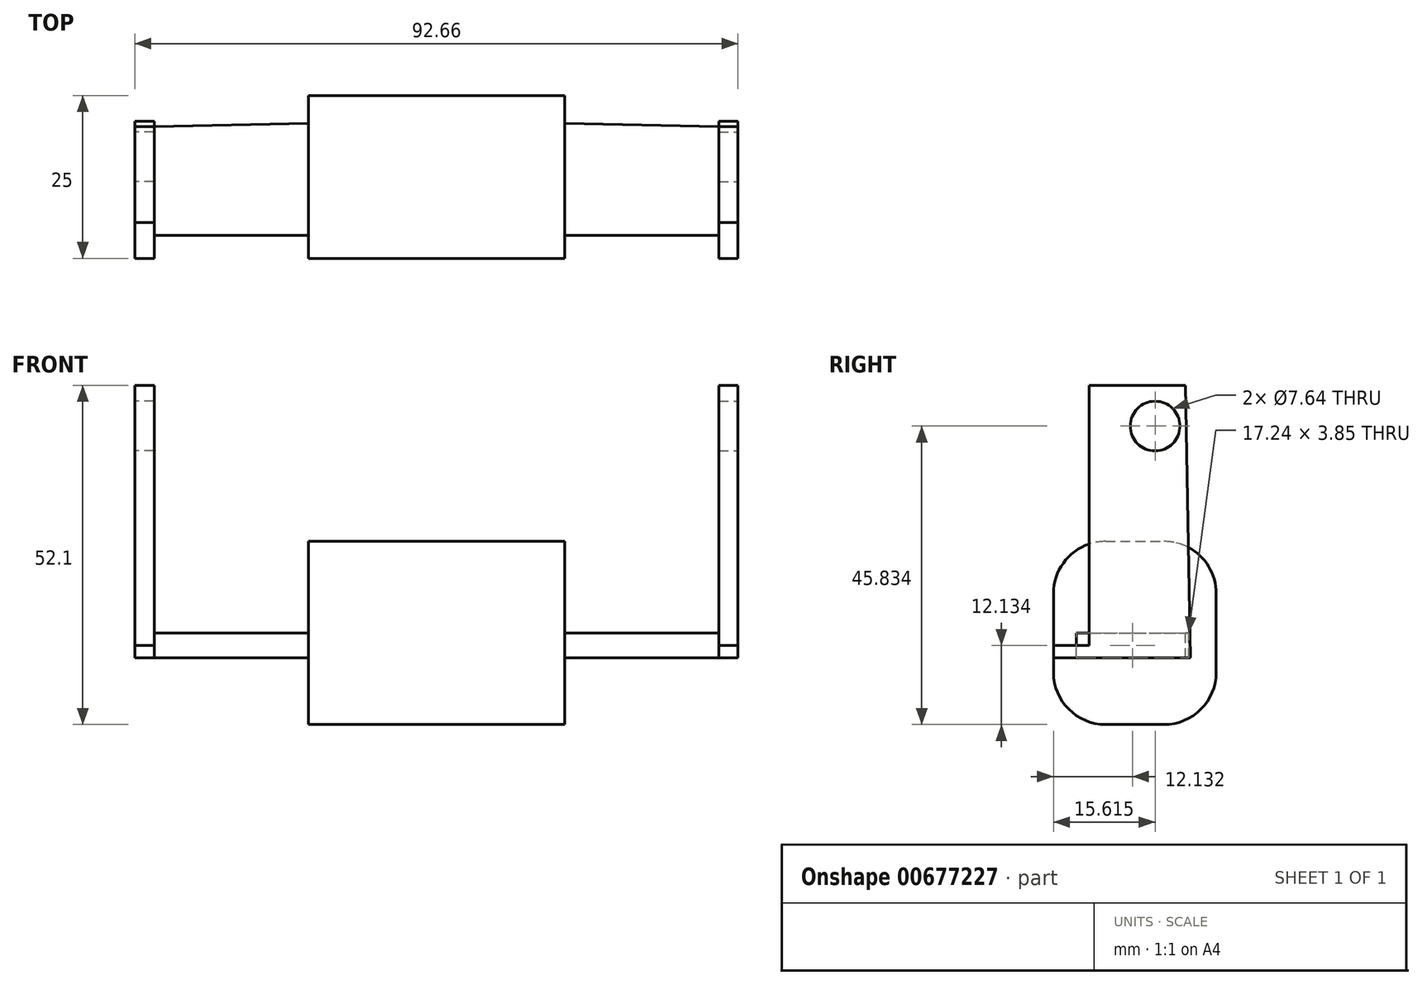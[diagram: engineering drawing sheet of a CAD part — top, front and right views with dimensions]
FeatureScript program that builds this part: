
annotation { "Feature Type Name" : "Feature", "Feature Type Description" : "" }
export const myFeature = defineFeature(function(context is Context, id is Id, definition is map)
    precondition{}
    {
        {
            var Q0;
            Q0=qCreatedBy(makeId("Front.planeOp"),FACE);
            var sketch = newSketch(context, id + "F0", { "sketchPlane" : qUnion([Q0])});
            skLineSegment(sketch, "E0", {"start": v(0, 17.91) * mm, "end": v(-19.69, 17.91) * mm});
            skLineSegment(sketch, "E1", {"start": v(-19.69, 17.91) * mm, "end": v(-19.69, -10.21) * mm});
            skLineSegment(sketch, "E2", {"start": v(-19.69, -10.21) * mm, "end": v(0, -10.21) * mm});
            skLineSegment(sketch, "E3", {"start": v(0, -10.21) * mm, "end": v(0, 17.91) * mm});
            skLineSegment(sketch, "E4", {"start": v(-19.69, 3.85) * mm, "end": v(-43.37, 3.85) * mm});
            skLineSegment(sketch, "E5", {"start": v(-43.37, 3.85) * mm, "end": v(-43.37, 41.9) * mm});
            skLineSegment(sketch, "E6", {"start": v(-43.37, 41.9) * mm, "end": v(-46.33, 41.9) * mm});
            skLineSegment(sketch, "E7", {"start": v(-46.33, 41.9) * mm, "end": v(-46.33, 0) * mm});
            skLineSegment(sketch, "E8", {"start": v(-46.33, 0) * mm, "end": v(-19.69, 0) * mm});
            skSolve(sketch);
        }
        {
            var Q0;
            Q0 = qSketchRegion(id + "F0", true);
            extrude(context, id + "F1", {"entities" : qUnion([Q0]), "depth" : 25 * mm, "offsetDistance" : 25 * mm});
        }
        {
            var Q0;
            Q0=makeQuery(id+"F1.opExtrude","CAP_EDGE",EDGE,{"disambiguationData":[OSD([sQuery(id+"F0.wireOp",EDGE,"E0")])],"isStart":true});
            var Q1;
            Q1=makeQuery(id+"F1.opExtrude","CAP_EDGE",EDGE,{"disambiguationData":[OSD([sQuery(id+"F0.wireOp",EDGE,"E2")])],"isStart":true});
            var Q2;
            Q2=makeQuery(id+"F1.opExtrude","CAP_EDGE",EDGE,{"disambiguationData":[OSD([sQuery(id+"F0.wireOp",EDGE,"E2")])],"isStart":false});
            var Q3;
            Q3=makeQuery(id+"F1.opExtrude","CAP_EDGE",EDGE,{"disambiguationData":[OSD([sQuery(id+"F0.wireOp",EDGE,"E0")])],"isStart":false});
            fillet(context, id + "F2", {"entities" : qUnion([Q0, Q1, Q2, Q3]), "radius" : 8 * mm, "tangentPropagation" : true, "allowEdgeOverflow" : false});
        }
        {
            var Q0;
            Q0=makeQuery(id+"F1.opExtrude","SWEPT_FACE",FACE,{"disambiguationData":[OSD([sQuery(id+"F0.wireOp",EDGE,"E4")])]});
            var sketch = newSketch(context, id + "F3", { "sketchPlane" : qUnion([Q0])});
            skLineSegment(sketch, "E9", {"start": v(-19.69, -21.49) * mm, "end": v(-43.37, -21.49) * mm});
            skLineSegment(sketch, "E10", {"start": v(-43.37, -21.49) * mm, "end": v(-43.37, -25) * mm});
            skLineSegment(sketch, "E11", {"start": v(-43.37, -25) * mm, "end": v(-19.69, -25) * mm});
            skLineSegment(sketch, "E12", {"start": v(-19.69, -25) * mm, "end": v(-19.69, -21.49) * mm});
            skLineSegment(sketch, "E13", {"start": v(-19.69, -4.25) * mm, "end": v(-43.37, -4.75) * mm});
            skLineSegment(sketch, "E14", {"start": v(-43.37, -4.75) * mm, "end": v(-43.37, 0) * mm});
            skLineSegment(sketch, "E15", {"start": v(-43.37, 0) * mm, "end": v(-20.53, 0) * mm});
            skLineSegment(sketch, "E16", {"start": v(-20.53, 0) * mm, "end": v(-19.69, 0) * mm});
            skLineSegment(sketch, "E17", {"start": v(-19.69, 0) * mm, "end": v(-19.69, -4.25) * mm});
            skSolve(sketch);
        }
        {
            var Q0;
            Q0 = qSketchRegion(id + "F3", true);
            extrude(context, id + "F4", {"entities" : qUnion([Q0]), "operationType" : NewBodyOperationType.REMOVE, "oppositeDirection" : true, "depth" : 25 * mm, "offsetDistance" : 25 * mm});
        }
        {
            var Q0;
            Q0=makeQuery(id+"F4.boolean.opBoolean","MERGE",FACE,{"derivedFrom":[makeQuery(id+"F1.opExtrude","SWEPT_FACE",FACE,{"disambiguationData":[OSD([sQuery(id+"F0.wireOp",EDGE,"E5")])]}),makeQuery(id+"F4.opExtrude","SWEPT_FACE",FACE,{"disambiguationData":[OSD([sQuery(id+"F3.wireOp",EDGE,"E10")])]}),makeQuery(id+"F4.opExtrude","SWEPT_FACE",FACE,{"disambiguationData":[OSD([sQuery(id+"F3.wireOp",EDGE,"E14")])]})]});
            var sketch = newSketch(context, id + "F5", { "sketchPlane" : qUnion([Q0])});
            skLineSegment(sketch, "E18", {"start": v(-25, 41.9) * mm, "end": v(-19.53, 41.9) * mm});
            skLineSegment(sketch, "E19", {"start": v(-19.53, 41.9) * mm, "end": v(-19.53, 1.92) * mm});
            skPoint(sketch, "E19.endSnap0", {"position": v(-21.49, 1.92) * mm});
            skLineSegment(sketch, "E20", {"start": v(-19.53, 1.92) * mm, "end": v(-25, 1.92) * mm});
            skLineSegment(sketch, "E21", {"start": v(-25, 1.92) * mm, "end": v(-25, 41.9) * mm});
            skLineSegment(sketch, "E22", {"start": v(-4.75, 41.9) * mm, "end": v(-3.94, 0) * mm});
            skLineSegment(sketch, "E23", {"start": v(-3.94, 0) * mm, "end": v(0, 0) * mm});
            skLineSegment(sketch, "E24", {"start": v(0, 0) * mm, "end": v(0, 40.74) * mm});
            skLineSegment(sketch, "E25", {"start": v(0, 40.74) * mm, "end": v(0, 41.9) * mm});
            skLineSegment(sketch, "E26", {"start": v(0, 41.9) * mm, "end": v(-4.75, 41.9) * mm});
            skSolve(sketch);
        }
        {
            var Q0;
            Q0 = qSketchRegion(id + "F5", true);
            extrude(context, id + "F6", {"entities" : qUnion([Q0]), "operationType" : NewBodyOperationType.REMOVE, "oppositeDirection" : true, "depth" : 25 * mm, "offsetDistance" : 25 * mm});
        }
        {
            var Q0;
            Q0=makeQuery(id+"F1.opExtrude","SWEPT_FACE",FACE,{"disambiguationData":[OSD([sQuery(id+"F0.wireOp",EDGE,"E7")])]});
            var sketch = newSketch(context, id + "F7", { "sketchPlane" : qUnion([Q0])});
            skCircle(sketch, "E27", {"center": v(9.39, 35.62) * mm, "radius": 3.82 * mm});
            skSolve(sketch);
        }
        {
            var Q0;
            Q0 = qSketchRegion(id + "F7", true);
            extrude(context, id + "F8", {"entities" : qUnion([Q0]), "operationType" : NewBodyOperationType.REMOVE, "oppositeDirection" : true, "depth" : 25 * mm, "offsetDistance" : 25 * mm});
        }
        {
            var Q0;
            Q0=makeQuery(id+"F1.opExtrude","SWEPT_BODY",BODY,{"disambiguationData":[OSD([sQuery(id+"F0.wireOp",EDGE,"E0"),sQuery(id+"F0.wireOp",EDGE,"E1"),sQuery(id+"F0.wireOp",EDGE,"E2"),sQuery(id+"F0.wireOp",EDGE,"E3"),sQuery(id+"F0.wireOp",EDGE,"E4"),sQuery(id+"F0.wireOp",EDGE,"E5"),sQuery(id+"F0.wireOp",EDGE,"E6"),sQuery(id+"F0.wireOp",EDGE,"E7"),sQuery(id+"F0.wireOp",EDGE,"E8")])]});
            var Q1;
            Q1=qCreatedBy(makeId("Right.planeOp"),FACE);
            mirror(context, id + "F9", {"operationType" : NewBodyOperationType.ADD, "entities" : qUnion([Q0]), "mirrorPlane" : qUnion([Q1])});
        }
    });
